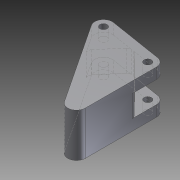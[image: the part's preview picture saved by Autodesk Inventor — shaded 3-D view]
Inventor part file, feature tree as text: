
AUTODESK INVENTOR PART (.ipt)
format: ipt  version: 2011 SP2 (Build 150309200, 309)  size: 134,144 bytes
history: native  units: mm
features: sketch x3, extrude x2, fillet x1, hole x1, projected_geometry x1
ambient origin geometry x8: Origin, YZ Plane, XZ Plane, XY Plane, X Axis, Y Axis, Z Axis, Center Point
bodies: Solid1 (feature_tree)
feature tree (8):
  extrude  "Extrusion1"  Depth=24.531041mm
  extrude  "Extrusion2"  Depth=4.0mm
  fillet  "Fillet1"  Radius=20.0mm
  hole  "Hole1"  [1 undecoded]
  sketch  "Sketch1"  dims[d0=32.752538mm d6=24.531041mm]
  sketch  "Sketch2"  dims[d14=43.915254mm d15=4.0mm d16=20.0mm d17=0.0mm]
  projected_geometry  "Projected Loop1"
  sketch  "Sketch3"  dims[d18=10.0mm d19=0.0mm d20=2.0mm d21=3.4mm d22=6.0mm d23=4.4mm d24=3.0mm d25=90.0deg d26=8.0mm d27=20.594885mm]
note: 1 required parameter value undecoded (feature->parameter linkage not recoverable at this tier; creation-order binding heuristic only, values carry confidence <= 0.55)
